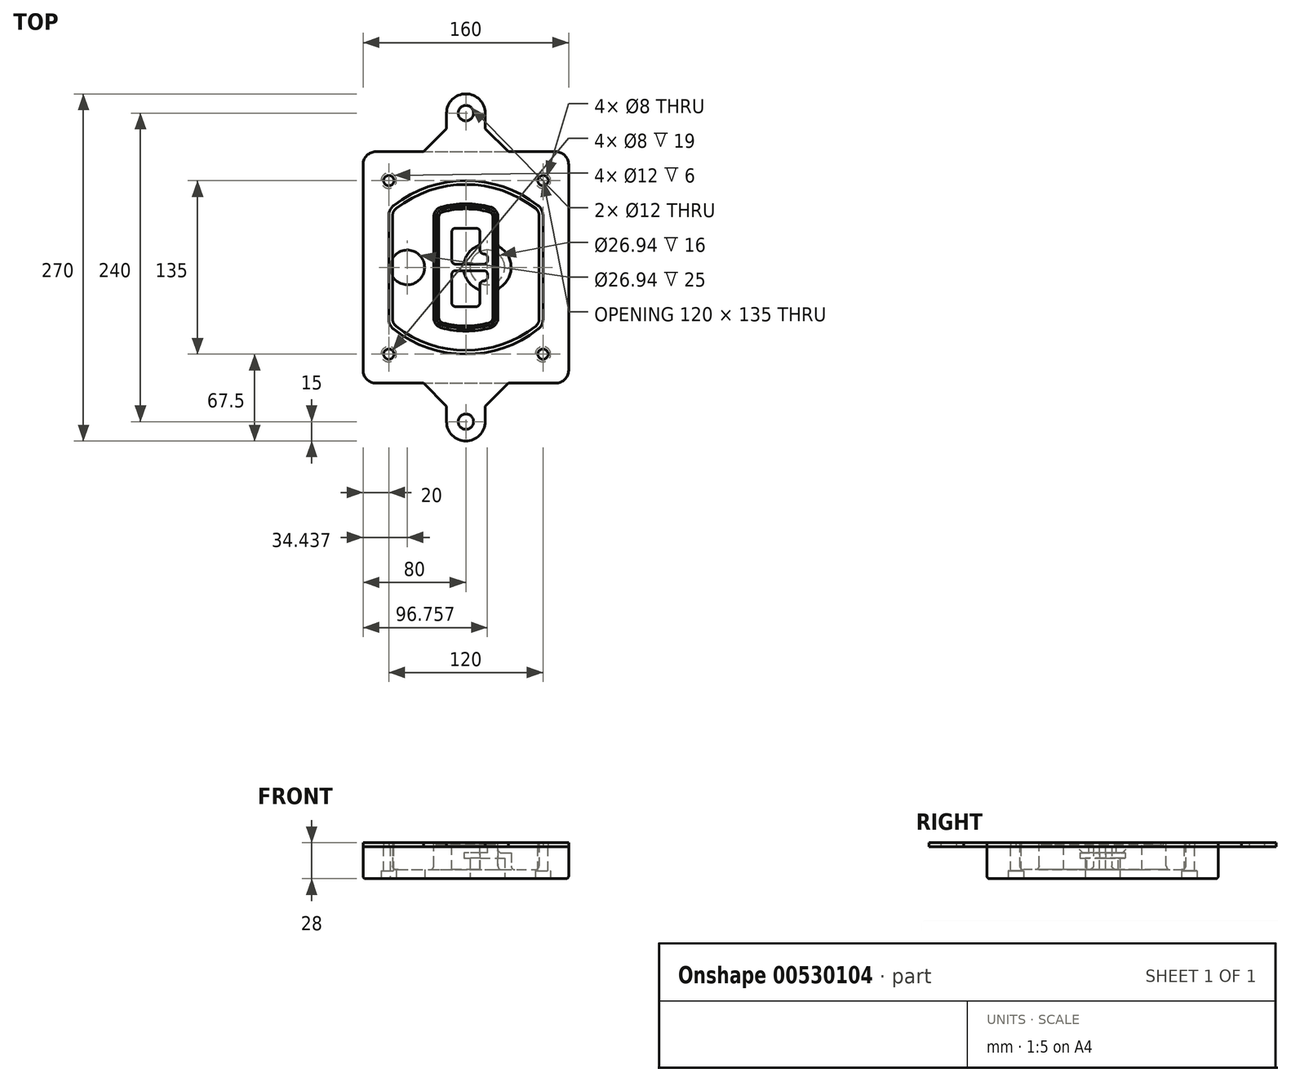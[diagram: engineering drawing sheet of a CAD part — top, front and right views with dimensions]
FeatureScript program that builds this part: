
annotation { "Feature Type Name" : "Feature", "Feature Type Description" : "" }
export const myFeature = defineFeature(function(context is Context, id is Id, definition is map)
    precondition{}
    {
        {
            var Q0;
            Q0=qCreatedBy(makeId("Top.planeOp"),FACE);
            var sketch = newSketch(context, id + "F0", { "sketchPlane" : qUnion([Q0])});
            skPoint(sketch, "E0.rect.middle", {"position": v(0, 0) * mm});
            skLineSegment(sketch, "E1.bottom", {"start": v(-70, -90) * mm, "end": v(70, -90) * mm});
            skLineSegment(sketch, "E1.top", {"start": v(-70, 90) * mm, "end": v(70, 90) * mm});
            skLineSegment(sketch, "E1.left", {"start": v(-80, -80) * mm, "end": v(-80, 80) * mm});
            skLineSegment(sketch, "E1.right", {"start": v(80, -80) * mm, "end": v(80, 80) * mm});
            skLineSegment(sketch, "E2", {"start": v(-80, 90) * mm, "end": v(80, -90) * mm, "construction": true});
            skLineSegment(sketch, "E3", {"start": v(80, 90) * mm, "end": v(-80, -90) * mm, "construction": true});
            skCircle(sketch, "E4", {"center": v(-60, 67.5) * mm, "radius": 4 * mm});
            skCircle(sketch, "E5", {"center": v(60, 67.5) * mm, "radius": 4 * mm});
            skCircle(sketch, "E6", {"center": v(60, -67.5) * mm, "radius": 4 * mm});
            skCircle(sketch, "E7", {"center": v(-60, -67.5) * mm, "radius": 4 * mm});
            skLineSegment(sketch, "E8", {"start": v(-60, 67.5) * mm, "end": v(60, 67.5) * mm, "construction": true});
            skLineSegment(sketch, "E9", {"start": v(60, 67.5) * mm, "end": v(60, -67.5) * mm, "construction": true});
            skLineSegment(sketch, "E10", {"start": v(60, -67.5) * mm, "end": v(-60, -67.5) * mm, "construction": true});
            skLineSegment(sketch, "E11", {"start": v(-60, -67.5) * mm, "end": v(-60, 67.5) * mm, "construction": true});
            skLineSegment(sketch, "E12", {"start": v(-60, 40.3) * mm, "end": v(-60, -40.3) * mm});
            skLineSegment(sketch, "E13", {"start": v(60, 40.3) * mm, "end": v(60, -40.3) * mm});
            skArc(sketch, "E14", {"start": v(56.15, 48.18) * mm, "mid": v(0, 67.5) * mm, "end": v(-56.15, 48.18) * mm});
            skArc(sketch, "E15", {"start": v(-56.15, -48.18) * mm, "mid": v(0, -67.5) * mm, "end": v(56.15, -48.18) * mm});
            skLineSegment(sketch, "E16", {"start": v(-60, 0) * mm, "end": v(60, 0) * mm, "construction": true});
            skPoint(sketch, "E17.visualSharp", {"position": v(-60, -45) * mm});
            skArc(sketch, "E17.filletArc", {"start": v(-60, -40.3) * mm, "mid": v(-58.99, -44.68) * mm, "end": v(-56.15, -48.18) * mm});
            skPoint(sketch, "E18.visualSharp", {"position": v(-60, 45) * mm});
            skArc(sketch, "E18.filletArc", {"start": v(-56.15, 48.18) * mm, "mid": v(-58.99, 44.68) * mm, "end": v(-60, 40.3) * mm});
            skPoint(sketch, "E19.visualSharp", {"position": v(60, 45) * mm});
            skArc(sketch, "E19.filletArc", {"start": v(60, 40.3) * mm, "mid": v(58.99, 44.68) * mm, "end": v(56.15, 48.18) * mm});
            skPoint(sketch, "E20.visualSharp", {"position": v(60, -45) * mm});
            skArc(sketch, "E20.filletArc", {"start": v(56.15, -48.18) * mm, "mid": v(58.99, -44.68) * mm, "end": v(60, -40.3) * mm});
            skPoint(sketch, "E21.visualSharp", {"position": v(-80, 90) * mm});
            skArc(sketch, "E21.filletArc", {"start": v(-70, 90) * mm, "mid": v(-77.07, 87.07) * mm, "end": v(-80, 80) * mm});
            skPoint(sketch, "E22.visualSharp", {"position": v(80, 90) * mm});
            skArc(sketch, "E22.filletArc", {"start": v(80, 80) * mm, "mid": v(77.07, 87.07) * mm, "end": v(70, 90) * mm});
            skPoint(sketch, "E23.visualSharp", {"position": v(80, -90) * mm});
            skArc(sketch, "E23.filletArc", {"start": v(70, -90) * mm, "mid": v(77.07, -87.07) * mm, "end": v(80, -80) * mm});
            skPoint(sketch, "E24.visualSharp", {"position": v(-80, -90) * mm});
            skArc(sketch, "E24.filletArc", {"start": v(-80, -80) * mm, "mid": v(-77.07, -87.07) * mm, "end": v(-70, -90) * mm});
            skArc(sketch, "E25.0", {"start": v(57, 40.3) * mm, "mid": v(56.3, 43.36) * mm, "end": v(54.3, 45.81) * mm});
            skLineSegment(sketch, "E25.1", {"start": v(57, 40.3) * mm, "end": v(57, -40.3) * mm});
            skArc(sketch, "E25.2", {"start": v(54.3, -45.81) * mm, "mid": v(56.3, -43.36) * mm, "end": v(57, -40.3) * mm});
            skArc(sketch, "E25.3", {"start": v(-54.3, -45.81) * mm, "mid": v(0, -64.5) * mm, "end": v(54.3, -45.81) * mm});
            skArc(sketch, "E25.4", {"start": v(-57, -40.3) * mm, "mid": v(-56.3, -43.36) * mm, "end": v(-54.3, -45.81) * mm});
            skArc(sketch, "E25.5", {"start": v(54.3, 45.81) * mm, "mid": v(0, 64.5) * mm, "end": v(-54.3, 45.81) * mm});
            skLineSegment(sketch, "E25.6", {"start": v(-57, 40.3) * mm, "end": v(-57, -40.3) * mm});
            skArc(sketch, "E25.7", {"start": v(-54.3, 45.81) * mm, "mid": v(-56.3, 43.36) * mm, "end": v(-57, 40.3) * mm});
            skArc(sketch, "E26.0", {"start": v(-58.62, 51.33) * mm, "mid": v(-62.58, 46.43) * mm, "end": v(-64, 40.3) * mm});
            skArc(sketch, "E26.1", {"start": v(58.62, 51.33) * mm, "mid": v(0, 71.5) * mm, "end": v(-58.62, 51.33) * mm});
            skArc(sketch, "E26.2", {"start": v(64, 40.3) * mm, "mid": v(62.58, 46.43) * mm, "end": v(58.62, 51.33) * mm});
            skLineSegment(sketch, "E26.3", {"start": v(64, 40.3) * mm, "end": v(64, -40.3) * mm});
            skArc(sketch, "E26.4", {"start": v(58.62, -51.33) * mm, "mid": v(62.58, -46.43) * mm, "end": v(64, -40.3) * mm});
            skLineSegment(sketch, "E26.5", {"start": v(-64, 40.3) * mm, "end": v(-64, -40.3) * mm});
            skArc(sketch, "E26.6", {"start": v(-58.62, -51.33) * mm, "mid": v(0, -71.5) * mm, "end": v(58.62, -51.33) * mm});
            skArc(sketch, "E26.7", {"start": v(-64, -40.3) * mm, "mid": v(-62.58, -46.43) * mm, "end": v(-58.62, -51.33) * mm});
            skSolve(sketch);
        }
        {
            var Q0;
            Q0=makeQuery(id+"F0.imprint","IMPRINT",FACE,{"disambiguationData":[TD([[makeQuery(id+"F0.imprint","IMPRINT",EDGE,{"derivedFrom":sQuery(id+"F0.wireOp",EDGE,"E1.bottom")}),1.0]])]});
            var Q1;
            Q1=makeQuery(id+"F0.imprint","IMPRINT",FACE,{"disambiguationData":[TD([[makeQuery(id+"F0.imprint","IMPRINT",EDGE,{"derivedFrom":sQuery(id+"F0.wireOp",EDGE,"E12")}),1.0]])]});
            var Q2;
            Q2=makeQuery(id+"F0.imprint","IMPRINT",FACE,{"disambiguationData":[TD([[makeQuery(id+"F0.imprint","IMPRINT",EDGE,{"derivedFrom":sQuery(id+"F0.wireOp",EDGE,"E25.0")}),1.0]])]});
            var Q3;
            Q3=makeQuery(id+"F0.imprint","IMPRINT",FACE,{"disambiguationData":[TD([[makeQuery(id+"F0.imprint","IMPRINT",EDGE,{"derivedFrom":sQuery(id+"F0.wireOp",EDGE,"E12")}),-1.0]])]});
            extrude(context, id + "F1", {"entities" : qUnion([Q0, Q1, Q2, Q3]), "oppositeDirection" : true, "depth" : 25 * mm});
        }
        {
            var Q0;
            Q0=makeQuery(id+"F0.imprint","IMPRINT",FACE,{"disambiguationData":[TD([[makeQuery(id+"F0.imprint","IMPRINT",EDGE,{"derivedFrom":sQuery(id+"F0.wireOp",EDGE,"E12")}),1.0]])]});
            extrude(context, id + "F2", {"entities" : qUnion([Q0]), "operationType" : NewBodyOperationType.ADD, "depth" : 3 * mm});
        }
        {
            var Q0;
            Q0=makeQuery(id+"F0.imprint","IMPRINT",FACE,{"disambiguationData":[TD([[makeQuery(id+"F0.imprint","IMPRINT",EDGE,{"derivedFrom":sQuery(id+"F0.wireOp",EDGE,"E25.0")}),1.0]])]});
            extrude(context, id + "F3", {"entities" : qUnion([Q0]), "operationType" : NewBodyOperationType.REMOVE, "oppositeDirection" : true, "depth" : 18 * mm});
        }
        {
            var Q0;
            Q0=makeQuery(id+"F2.opExtrude","CAP_FACE",FACE,{"disambiguationData":[OSD([sQuery(id+"F0.wireOp",EDGE,"E12"),sQuery(id+"F0.wireOp",EDGE,"E13"),sQuery(id+"F0.wireOp",EDGE,"E14"),sQuery(id+"F0.wireOp",EDGE,"E15"),sQuery(id+"F0.wireOp",EDGE,"E17.filletArc"),sQuery(id+"F0.wireOp",EDGE,"E18.filletArc"),sQuery(id+"F0.wireOp",EDGE,"E19.filletArc"),sQuery(id+"F0.wireOp",EDGE,"E20.filletArc"),sQuery(id+"F0.wireOp",EDGE,"E25.0"),sQuery(id+"F0.wireOp",EDGE,"E25.1"),sQuery(id+"F0.wireOp",EDGE,"E25.2"),sQuery(id+"F0.wireOp",EDGE,"E25.3"),sQuery(id+"F0.wireOp",EDGE,"E25.4"),sQuery(id+"F0.wireOp",EDGE,"E25.5"),sQuery(id+"F0.wireOp",EDGE,"E25.6"),sQuery(id+"F0.wireOp",EDGE,"E25.7")])],"isStart":false});
            var sketch = newSketch(context, id + "F4", { "sketchPlane" : qUnion([Q0])});
            skArc(sketch, "E27.0", {"start": v(-19.08, -46.97) * mm, "mid": v(0, -49.5) * mm, "end": v(19.08, -46.97) * mm});
            skArc(sketch, "E28.0", {"start": v(19.08, 46.97) * mm, "mid": v(0, 49.5) * mm, "end": v(-19.08, 46.97) * mm});
            skLineSegment(sketch, "E29", {"start": v(-25, 39.25) * mm, "end": v(-25, -39.25) * mm});
            skLineSegment(sketch, "E30", {"start": v(25, 39.25) * mm, "end": v(25, -39.25) * mm});
            skLineSegment(sketch, "E31", {"start": v(-25, 45.1) * mm, "end": v(25, 45.1) * mm, "construction": true});
            skLineSegment(sketch, "E32", {"start": v(-25, -45.1) * mm, "end": v(25, -45.1) * mm, "construction": true});
            skPoint(sketch, "E33.visualSharp", {"position": v(-25, 45.1) * mm});
            skArc(sketch, "E33.filletArc", {"start": v(-19.08, 46.97) * mm, "mid": v(-23.35, 44.11) * mm, "end": v(-25, 39.25) * mm});
            skPoint(sketch, "E34.visualSharp", {"position": v(25, 45.1) * mm});
            skArc(sketch, "E34.filletArc", {"start": v(25, 39.25) * mm, "mid": v(23.35, 44.11) * mm, "end": v(19.08, 46.97) * mm});
            skPoint(sketch, "E35.visualSharp", {"position": v(25, -45.1) * mm});
            skArc(sketch, "E35.filletArc", {"start": v(19.08, -46.97) * mm, "mid": v(23.35, -44.11) * mm, "end": v(25, -39.25) * mm});
            skPoint(sketch, "E36.visualSharp", {"position": v(-25, -45.1) * mm});
            skArc(sketch, "E36.filletArc", {"start": v(-25, -39.25) * mm, "mid": v(-23.35, -44.11) * mm, "end": v(-19.08, -46.97) * mm});
            skArc(sketch, "E37.0", {"start": v(54.3, 45.81) * mm, "mid": v(0, 64.5) * mm, "end": v(-54.3, 45.81) * mm});
            skArc(sketch, "E37.1", {"start": v(-54.3, 45.81) * mm, "mid": v(-56.3, 43.36) * mm, "end": v(-57, 40.3) * mm});
            skLineSegment(sketch, "E37.2", {"start": v(-57, 40.3) * mm, "end": v(-57, -40.3) * mm});
            skArc(sketch, "E37.3", {"start": v(-57, -40.3) * mm, "mid": v(-56.3, -43.36) * mm, "end": v(-54.3, -45.81) * mm});
            skArc(sketch, "E37.4", {"start": v(-54.3, -45.81) * mm, "mid": v(0, -64.5) * mm, "end": v(54.3, -45.81) * mm});
            skArc(sketch, "E37.5", {"start": v(54.3, -45.81) * mm, "mid": v(56.3, -43.36) * mm, "end": v(57, -40.3) * mm});
            skLineSegment(sketch, "E37.6", {"start": v(57, 40.3) * mm, "end": v(57, -40.3) * mm});
            skArc(sketch, "E37.7", {"start": v(57, 40.3) * mm, "mid": v(56.3, 43.36) * mm, "end": v(54.3, 45.81) * mm});
            skLineSegment(sketch, "E38.0", {"start": v(23, 39.25) * mm, "end": v(23, -39.25) * mm});
            skArc(sketch, "E38.1", {"start": v(18.56, -45.04) * mm, "mid": v(21.76, -42.9) * mm, "end": v(23, -39.25) * mm});
            skArc(sketch, "E38.2", {"start": v(-18.56, -45.04) * mm, "mid": v(0, -47.5) * mm, "end": v(18.56, -45.04) * mm});
            skArc(sketch, "E38.3", {"start": v(-23, -39.25) * mm, "mid": v(-21.76, -42.9) * mm, "end": v(-18.56, -45.04) * mm});
            skLineSegment(sketch, "E38.4", {"start": v(-23, 39.25) * mm, "end": v(-23, -39.25) * mm});
            skArc(sketch, "E38.5", {"start": v(23, 39.25) * mm, "mid": v(21.76, 42.9) * mm, "end": v(18.56, 45.04) * mm});
            skArc(sketch, "E38.6", {"start": v(-18.56, 45.04) * mm, "mid": v(-21.76, 42.9) * mm, "end": v(-23, 39.25) * mm});
            skArc(sketch, "E38.7", {"start": v(18.56, 45.04) * mm, "mid": v(0, 47.5) * mm, "end": v(-18.56, 45.04) * mm});
            skArc(sketch, "E39.0", {"start": v(21, 39.25) * mm, "mid": v(20.18, 41.68) * mm, "end": v(18.04, 43.1) * mm});
            skLineSegment(sketch, "E39.1", {"start": v(21, 39.25) * mm, "end": v(21, -39.25) * mm});
            skArc(sketch, "E39.2", {"start": v(18.04, -43.1) * mm, "mid": v(20.18, -41.68) * mm, "end": v(21, -39.25) * mm});
            skArc(sketch, "E39.3", {"start": v(-18.04, -43.1) * mm, "mid": v(0, -45.5) * mm, "end": v(18.04, -43.1) * mm});
            skArc(sketch, "E39.4", {"start": v(-21, -39.25) * mm, "mid": v(-20.18, -41.68) * mm, "end": v(-18.04, -43.1) * mm});
            skArc(sketch, "E39.5", {"start": v(18.04, 43.1) * mm, "mid": v(0, 45.5) * mm, "end": v(-18.04, 43.1) * mm});
            skLineSegment(sketch, "E39.6", {"start": v(-21, 39.25) * mm, "end": v(-21, -39.25) * mm});
            skArc(sketch, "E39.7", {"start": v(-18.04, 43.1) * mm, "mid": v(-20.18, 41.68) * mm, "end": v(-21, 39.25) * mm});
            skLineSegment(sketch, "E40", {"start": v(-25, 0) * mm, "end": v(25, 0) * mm, "construction": true});
            skLineSegment(sketch, "E41", {"start": v(-11, 5.5) * mm, "end": v(-11, 27.5) * mm});
            skLineSegment(sketch, "E42", {"start": v(-8, 30.5) * mm, "end": v(8, 30.5) * mm});
            skLineSegment(sketch, "E43", {"start": v(11, 27.5) * mm, "end": v(11, 13.5) * mm});
            skLineSegment(sketch, "E44", {"start": v(14, 10.5) * mm, "end": v(14, 10.5) * mm});
            skLineSegment(sketch, "E45", {"start": v(17, 7.5) * mm, "end": v(17, 5.5) * mm});
            skLineSegment(sketch, "E46", {"start": v(14, 2.5) * mm, "end": v(-8, 2.5) * mm});
            skPoint(sketch, "E47.visualSharp", {"position": v(-11, 30.5) * mm});
            skArc(sketch, "E47.filletArc", {"start": v(-8, 30.5) * mm, "mid": v(-10.12, 29.62) * mm, "end": v(-11, 27.5) * mm});
            skPoint(sketch, "E48.visualSharp", {"position": v(11, 30.5) * mm});
            skArc(sketch, "E48.filletArc", {"start": v(11, 27.5) * mm, "mid": v(10.12, 29.62) * mm, "end": v(8, 30.5) * mm});
            skPoint(sketch, "E49.visualSharp", {"position": v(11, 10.5) * mm});
            skArc(sketch, "E49.filletArc", {"start": v(11, 13.5) * mm, "mid": v(11.88, 11.38) * mm, "end": v(14, 10.5) * mm});
            skPoint(sketch, "E50.visualSharp", {"position": v(17, 10.5) * mm});
            skArc(sketch, "E50.filletArc", {"start": v(17, 7.5) * mm, "mid": v(16.12, 9.62) * mm, "end": v(14, 10.5) * mm});
            skPoint(sketch, "E51.visualSharp", {"position": v(17, 2.5) * mm});
            skArc(sketch, "E51.filletArc", {"start": v(14, 2.5) * mm, "mid": v(16.12, 3.38) * mm, "end": v(17, 5.5) * mm});
            skPoint(sketch, "E52.visualSharp", {"position": v(-11, 2.5) * mm});
            skArc(sketch, "E52.filletArc", {"start": v(-11, 5.5) * mm, "mid": v(-10.12, 3.38) * mm, "end": v(-8, 2.5) * mm});
            skLineSegment(sketch, "E53.0.MirrorCS", {"start": v(14, -2.5) * mm, "end": v(-8, -2.5) * mm});
            skArc(sketch, "E54.0.MirrorCS", {"start": v(-11, -5.5) * mm, "mid": v(-10.12, -3.38) * mm, "end": v(-8, -2.5) * mm});
            skLineSegment(sketch, "E55.0.MirrorCS", {"start": v(-11, -5.5) * mm, "end": v(-11, -27.5) * mm});
            skArc(sketch, "E56.0.MirrorCS", {"start": v(-8, -30.5) * mm, "mid": v(-10.12, -29.62) * mm, "end": v(-11, -27.5) * mm});
            skLineSegment(sketch, "E57.0.MirrorCS", {"start": v(-8, -30.5) * mm, "end": v(8, -30.5) * mm});
            skArc(sketch, "E58.0.MirrorCS", {"start": v(11, -27.5) * mm, "mid": v(10.12, -29.62) * mm, "end": v(8, -30.5) * mm});
            skLineSegment(sketch, "E59.0.MirrorCS", {"start": v(11, -27.5) * mm, "end": v(11, -13.5) * mm});
            skArc(sketch, "E60.0.MirrorCS", {"start": v(11, -13.5) * mm, "mid": v(11.88, -11.38) * mm, "end": v(14, -10.5) * mm});
            skArc(sketch, "E61.0.MirrorCS", {"start": v(17, -7.5) * mm, "mid": v(16.12, -9.62) * mm, "end": v(14, -10.5) * mm});
            skLineSegment(sketch, "E62.0.MirrorCS", {"start": v(17, -7.5) * mm, "end": v(17, -5.5) * mm});
            skArc(sketch, "E63.0.MirrorCS", {"start": v(14, -2.5) * mm, "mid": v(16.12, -3.38) * mm, "end": v(17, -5.5) * mm});
            skSolve(sketch);
        }
        {
            var Q0;
            Q0=makeQuery(id+"F4.imprint","IMPRINT",FACE,{"disambiguationData":[TD([[makeQuery(id+"F4.imprint","IMPRINT",EDGE,{"derivedFrom":sQuery(id+"F4.wireOp",EDGE,"E27.0")}),1.0]])]});
            var Q1;
            Q1=makeQuery(id+"F4.imprint","IMPRINT",FACE,{"disambiguationData":[TD([[makeQuery(id+"F4.imprint","IMPRINT",EDGE,{"derivedFrom":sQuery(id+"F4.wireOp",EDGE,"E38.0")}),-1.0]])]});
            var Q2;
            Q2=makeQuery(id+"F4.imprint","IMPRINT",FACE,{"disambiguationData":[TD([[makeQuery(id+"F4.imprint","IMPRINT",EDGE,{"derivedFrom":sQuery(id+"F4.wireOp",EDGE,"E39.0")}),1.0]])]});
            extrude(context, id + "F5", {"entities" : qUnion([Q0, Q1, Q2]), "operationType" : NewBodyOperationType.ADD, "endBound" : BoundingType.UP_TO_NEXT, "oppositeDirection" : true, "depth" : 25 * mm});
        }
        {
            var Q0;
            Q0=makeQuery(id+"F4.imprint","IMPRINT",FACE,{"disambiguationData":[TD([[makeQuery(id+"F4.imprint","IMPRINT",EDGE,{"derivedFrom":sQuery(id+"F4.wireOp",EDGE,"E38.0")}),-1.0]])]});
            extrude(context, id + "F6", {"entities" : qUnion([Q0]), "operationType" : NewBodyOperationType.REMOVE, "oppositeDirection" : true, "depth" : 2 * mm});
        }
        {
            var Q0;
            Q0=makeQuery(id+"F1.opExtrude","CAP_FACE",FACE,{"disambiguationData":[OSD([sQuery(id+"F0.wireOp",EDGE,"E1.bottom"),sQuery(id+"F0.wireOp",EDGE,"E1.top"),sQuery(id+"F0.wireOp",EDGE,"E1.left"),sQuery(id+"F0.wireOp",EDGE,"E1.right"),sQuery(id+"F0.wireOp",EDGE,"E4"),sQuery(id+"F0.wireOp",EDGE,"E5"),sQuery(id+"F0.wireOp",EDGE,"E6"),sQuery(id+"F0.wireOp",EDGE,"E7"),sQuery(id+"F0.wireOp",EDGE,"E21.filletArc"),sQuery(id+"F0.wireOp",EDGE,"E22.filletArc"),sQuery(id+"F0.wireOp",EDGE,"E23.filletArc"),sQuery(id+"F0.wireOp",EDGE,"E24.filletArc")])],"isStart":false});
            var sketch = newSketch(context, id + "F7", { "sketchPlane" : qUnion([Q0])});
            skCircle(sketch, "E64", {"center": v(16.76, 0) * mm, "radius": 13.47 * mm});
            skCircle(sketch, "E65", {"center": v(-45.56, 0) * mm, "radius": 13.47 * mm});
            skLineSegment(sketch, "E66", {"start": v(80, 0) * mm, "end": v(-80, 0) * mm});
            skCircle(sketch, "E67", {"center": v(16.76, 0) * mm, "radius": 18.47 * mm});
            skCircle(sketch, "E68", {"center": v(60, -67.5) * mm, "radius": 6 * mm});
            skCircle(sketch, "E69", {"center": v(-60, -67.5) * mm, "radius": 6 * mm});
            skCircle(sketch, "E70", {"center": v(-60, 67.5) * mm, "radius": 6 * mm});
            skCircle(sketch, "E71", {"center": v(60, 67.5) * mm, "radius": 6 * mm});
            skSolve(sketch);
        }
        {
            var Q0;
            {var subQ1=sQuery(id+"F7.wireOp",EDGE,"E66");var subQ4=sQuery(id+"F7.wireOp",EDGE,"E64");var subQ6=makeQuery(id+"F7.imprint","INTERSECT",VERTEX,{"disambiguationData":[OD(0.0)],"derivedFrom":[subQ4,subQ1]});Q0=makeQuery(id+"F7.imprint","IMPRINT",FACE,{"disambiguationData":[TD([[makeQuery(id+"F7.imprint","IMPRINT",EDGE,{"disambiguationData":[TD([[subQ6,-1.0]])],"derivedFrom":subQ4}),-1.0]])]});}
            var Q1;
            {var subQ0=sQuery(id+"F7.wireOp",EDGE,"E66");var subQ1=sQuery(id+"F7.wireOp",EDGE,"E64");var subQ3=makeQuery(id+"F7.imprint","INTERSECT",VERTEX,{"disambiguationData":[OD(0.0)],"derivedFrom":[subQ1,subQ0]});Q1=makeQuery(id+"F7.imprint","IMPRINT",FACE,{"disambiguationData":[TD([[makeQuery(id+"F7.imprint","IMPRINT",EDGE,{"disambiguationData":[TD([[subQ3,-1.0]])],"derivedFrom":subQ1}),1.0]])]});}
            var Q2;
            {var subQ0=sQuery(id+"F7.wireOp",EDGE,"E66");var subQ1=sQuery(id+"F7.wireOp",EDGE,"E64");var subQ3=makeQuery(id+"F7.imprint","INTERSECT",VERTEX,{"disambiguationData":[OD(0.0)],"derivedFrom":[subQ1,subQ0]});Q2=makeQuery(id+"F7.imprint","IMPRINT",FACE,{"disambiguationData":[TD([[makeQuery(id+"F7.imprint","IMPRINT",EDGE,{"disambiguationData":[TD([[subQ3,1.0]])],"derivedFrom":subQ1}),1.0]])]});}
            var Q3;
            {var subQ1=sQuery(id+"F7.wireOp",EDGE,"E66");var subQ4=sQuery(id+"F7.wireOp",EDGE,"E64");var subQ6=makeQuery(id+"F7.imprint","INTERSECT",VERTEX,{"disambiguationData":[OD(0.0)],"derivedFrom":[subQ4,subQ1]});Q3=makeQuery(id+"F7.imprint","IMPRINT",FACE,{"disambiguationData":[TD([[makeQuery(id+"F7.imprint","IMPRINT",EDGE,{"disambiguationData":[TD([[subQ6,1.0]])],"derivedFrom":subQ4}),-1.0]])]});}
            extrude(context, id + "F8", {"entities" : qUnion([Q0, Q1, Q2, Q3]), "operationType" : NewBodyOperationType.ADD, "oppositeDirection" : true, "depth" : 20 * mm});
        }
        {
            var Q0;
            {var subQ0=sQuery(id+"F7.wireOp",EDGE,"E66");var subQ1=sQuery(id+"F7.wireOp",EDGE,"E64");var subQ3=makeQuery(id+"F7.imprint","INTERSECT",VERTEX,{"disambiguationData":[OD(0.0)],"derivedFrom":[subQ1,subQ0]});Q0=makeQuery(id+"F7.imprint","IMPRINT",FACE,{"disambiguationData":[TD([[makeQuery(id+"F7.imprint","IMPRINT",EDGE,{"disambiguationData":[TD([[subQ3,-1.0]])],"derivedFrom":subQ1}),1.0]])]});}
            var Q1;
            {var subQ0=sQuery(id+"F7.wireOp",EDGE,"E66");var subQ1=sQuery(id+"F7.wireOp",EDGE,"E64");var subQ3=makeQuery(id+"F7.imprint","INTERSECT",VERTEX,{"disambiguationData":[OD(0.0)],"derivedFrom":[subQ1,subQ0]});Q1=makeQuery(id+"F7.imprint","IMPRINT",FACE,{"disambiguationData":[TD([[makeQuery(id+"F7.imprint","IMPRINT",EDGE,{"disambiguationData":[TD([[subQ3,1.0]])],"derivedFrom":subQ1}),1.0]])]});}
            extrude(context, id + "F9", {"entities" : qUnion([Q0, Q1]), "operationType" : NewBodyOperationType.REMOVE, "oppositeDirection" : true, "depth" : 16 * mm});
        }
        {
            var Q0;
            {var subQ0=sQuery(id+"F7.wireOp",EDGE,"E66");var subQ1=sQuery(id+"F7.wireOp",EDGE,"E65");var subQ3=makeQuery(id+"F7.imprint","INTERSECT",VERTEX,{"disambiguationData":[OD(0.0)],"derivedFrom":[subQ1,subQ0]});Q0=makeQuery(id+"F7.imprint","IMPRINT",FACE,{"disambiguationData":[TD([[makeQuery(id+"F7.imprint","IMPRINT",EDGE,{"disambiguationData":[TD([[subQ3,-1.0]])],"derivedFrom":subQ1}),1.0]])]});}
            var Q1;
            {var subQ0=sQuery(id+"F7.wireOp",EDGE,"E66");var subQ1=sQuery(id+"F7.wireOp",EDGE,"E65");var subQ3=makeQuery(id+"F7.imprint","INTERSECT",VERTEX,{"disambiguationData":[OD(0.0)],"derivedFrom":[subQ1,subQ0]});Q1=makeQuery(id+"F7.imprint","IMPRINT",FACE,{"disambiguationData":[TD([[makeQuery(id+"F7.imprint","IMPRINT",EDGE,{"disambiguationData":[TD([[subQ3,1.0]])],"derivedFrom":subQ1}),1.0]])]});}
            extrude(context, id + "F10", {"entities" : qUnion([Q0, Q1]), "operationType" : NewBodyOperationType.REMOVE, "oppositeDirection" : true, "depth" : 25 * mm});
        }
        {
            var Q0;
            Q0=makeQuery(id+"F7.imprint","IMPRINT",FACE,{"disambiguationData":[TD([[makeQuery(id+"F7.imprint","IMPRINT",EDGE,{"derivedFrom":sQuery(id+"F7.wireOp",EDGE,"E68")}),1.0]])]});
            var Q1;
            Q1=makeQuery(id+"F7.imprint","IMPRINT",FACE,{"disambiguationData":[TD([[makeQuery(id+"F7.imprint","IMPRINT",EDGE,{"derivedFrom":makeQuery(id+"F1.opExtrude","CAP_EDGE",EDGE,{"disambiguationData":[OSD([sQuery(id+"F0.wireOp",EDGE,"E5")])],"isStart":false})}),-1.0]])]});
            var Q2;
            Q2=makeQuery(id+"F7.imprint","IMPRINT",FACE,{"disambiguationData":[TD([[makeQuery(id+"F7.imprint","IMPRINT",EDGE,{"derivedFrom":sQuery(id+"F7.wireOp",EDGE,"E69")}),1.0]])]});
            var Q3;
            Q3=makeQuery(id+"F7.imprint","IMPRINT",FACE,{"disambiguationData":[TD([[makeQuery(id+"F7.imprint","IMPRINT",EDGE,{"derivedFrom":makeQuery(id+"F1.opExtrude","CAP_EDGE",EDGE,{"disambiguationData":[OSD([sQuery(id+"F0.wireOp",EDGE,"E4")])],"isStart":false})}),-1.0]])]});
            var Q4;
            Q4=makeQuery(id+"F7.imprint","IMPRINT",FACE,{"disambiguationData":[TD([[makeQuery(id+"F7.imprint","IMPRINT",EDGE,{"derivedFrom":sQuery(id+"F7.wireOp",EDGE,"E70")}),1.0]])]});
            var Q5;
            Q5=makeQuery(id+"F7.imprint","IMPRINT",FACE,{"disambiguationData":[TD([[makeQuery(id+"F7.imprint","IMPRINT",EDGE,{"derivedFrom":makeQuery(id+"F1.opExtrude","CAP_EDGE",EDGE,{"disambiguationData":[OSD([sQuery(id+"F0.wireOp",EDGE,"E7")])],"isStart":false})}),-1.0]])]});
            var Q6;
            Q6=makeQuery(id+"F7.imprint","IMPRINT",FACE,{"disambiguationData":[TD([[makeQuery(id+"F7.imprint","IMPRINT",EDGE,{"derivedFrom":sQuery(id+"F7.wireOp",EDGE,"E71")}),1.0]])]});
            var Q7;
            Q7=makeQuery(id+"F7.imprint","IMPRINT",FACE,{"disambiguationData":[TD([[makeQuery(id+"F7.imprint","IMPRINT",EDGE,{"derivedFrom":makeQuery(id+"F1.opExtrude","CAP_EDGE",EDGE,{"disambiguationData":[OSD([sQuery(id+"F0.wireOp",EDGE,"E6")])],"isStart":false})}),-1.0]])]});
            extrude(context, id + "F11", {"entities" : qUnion([Q0, Q1, Q2, Q3, Q4, Q5, Q6, Q7]), "operationType" : NewBodyOperationType.REMOVE, "oppositeDirection" : true, "depth" : 6 * mm});
        }
        {
            var Q0;
            Q0=makeQuery(id+"F9.boolean.opBoolean","COPY",FACE,{"derivedFrom":makeQuery(id+"F9.opExtrude","CAP_FACE",FACE,{"disambiguationData":[OSD([sQuery(id+"F7.wireOp",EDGE,"E64")])],"isStart":false})});
            var sketch = newSketch(context, id + "F12", { "sketchPlane" : qUnion([Q0])});
            skArc(sketch, "E72.0", {"start": v(11, 17.55) * mm, "mid": v(2.57, 11.82) * mm, "end": v(-1.54, 2.5) * mm});
            skArc(sketch, "E72.1", {"start": v(-1.54, -2.5) * mm, "mid": v(2.57, -11.82) * mm, "end": v(11, -17.55) * mm});
            skLineSegment(sketch, "E73", {"start": v(-1.54, -2.5) * mm, "end": v(14, -2.5) * mm});
            skLineSegment(sketch, "E74.0", {"start": v(14, 2.5) * mm, "end": v(-1.54, 2.5) * mm});
            skArc(sketch, "E74.1", {"start": v(14, 2.5) * mm, "mid": v(16.12, 3.38) * mm, "end": v(17, 5.5) * mm});
            skLineSegment(sketch, "E74.2", {"start": v(17, 7.5) * mm, "end": v(17, 5.5) * mm});
            skArc(sketch, "E74.3", {"start": v(17, 7.5) * mm, "mid": v(16.12, 9.62) * mm, "end": v(14, 10.5) * mm});
            skArc(sketch, "E74.4", {"start": v(11, 13.5) * mm, "mid": v(11.88, 11.38) * mm, "end": v(14, 10.5) * mm});
            skLineSegment(sketch, "E74.5", {"start": v(11, 17.55) * mm, "end": v(11, 13.5) * mm});
            skLineSegment(sketch, "E74.7", {"start": v(14, -2.5) * mm, "end": v(-1.54, -2.5) * mm});
            skArc(sketch, "E74.8", {"start": v(14, -2.5) * mm, "mid": v(16.12, -3.38) * mm, "end": v(17, -5.5) * mm});
            skLineSegment(sketch, "E74.9", {"start": v(17, -7.5) * mm, "end": v(17, -5.5) * mm});
            skArc(sketch, "E74.10", {"start": v(17, -7.5) * mm, "mid": v(16.12, -9.62) * mm, "end": v(14, -10.5) * mm});
            skArc(sketch, "E74.11", {"start": v(11, -13.5) * mm, "mid": v(11.88, -11.38) * mm, "end": v(14, -10.5) * mm});
            skLineSegment(sketch, "E74.12", {"start": v(11, -17.55) * mm, "end": v(11, -13.5) * mm});
            skPoint(sketch, "E75.orphan", {"position": v(11, -27.5) * mm});
            skPoint(sketch, "E76.orphan", {"position": v(-8, -2.5) * mm});
            skPoint(sketch, "E77.orphan", {"position": v(-8, 2.5) * mm});
            skPoint(sketch, "E78.orphan", {"position": v(11, 27.5) * mm});
            skSolve(sketch);
        }
        {
            var Q0;
            {var subQ7=sQuery(id+"F12.wireOp",EDGE,"E72.0");var subQ14=sQuery(id+"F12.wireOp",EDGE,"E72.1");var subQ16=sQuery(id+"F12.wireOp",EDGE,"E74.1");var subQ18=sQuery(id+"F12.wireOp",EDGE,"E74.8");Q0=qUnion([makeQuery(id+"F12.imprint","IMPRINT",FACE,{"disambiguationData":[TD([[makeQuery(id+"F12.imprint","IMPRINT",EDGE,{"derivedFrom":subQ7}),1.0]])]}),makeQuery(id+"F12.imprint","IMPRINT",FACE,{"disambiguationData":[TD([[makeQuery(id+"F12.imprint","IMPRINT",EDGE,{"derivedFrom":subQ14}),1.0]])]}),makeQuery(id+"F12.imprint","IMPRINT",FACE,{"disambiguationData":[TD([[makeQuery(id+"F12.imprint","IMPRINT",EDGE,{"derivedFrom":subQ16}),1.0]])]}),makeQuery(id+"F12.imprint","IMPRINT",FACE,{"disambiguationData":[TD([[makeQuery(id+"F12.imprint","IMPRINT",EDGE,{"derivedFrom":subQ18}),-1.0]])]})]);}
            var Q1;
            Q1=makeQuery(id+"F5.boolean.opBoolean","SPLIT",FACE,{"disambiguationData":[TD([makeQuery(id+"F5.opExtrude","SWEPT_FACE",FACE,{"disambiguationData":[OSD([sQuery(id+"F4.wireOp",EDGE,"E41")])]})])],"derivedFrom":makeQuery(id+"F3.boolean.opBoolean","COPY",FACE,{"derivedFrom":makeQuery(id+"F3.opExtrude","CAP_FACE",FACE,{"disambiguationData":[OSD([sQuery(id+"F0.wireOp",EDGE,"E25.0"),sQuery(id+"F0.wireOp",EDGE,"E25.1"),sQuery(id+"F0.wireOp",EDGE,"E25.2"),sQuery(id+"F0.wireOp",EDGE,"E25.3"),sQuery(id+"F0.wireOp",EDGE,"E25.4"),sQuery(id+"F0.wireOp",EDGE,"E25.5"),sQuery(id+"F0.wireOp",EDGE,"E25.6"),sQuery(id+"F0.wireOp",EDGE,"E25.7")])],"isStart":false})})});
            extrude(context, id + "F13", {"entities" : qUnion([Q0]), "operationType" : NewBodyOperationType.REMOVE, "endBound" : BoundingType.UP_TO_SURFACE, "endBoundEntityFace" : qUnion([Q1]), "depth" : 25 * mm});
        }
        {
            var Q0;
            Q0=makeQuery(id+"F3.boolean.opBoolean","COPY",EDGE,{"derivedFrom":makeQuery(id+"F3.opExtrude","CAP_EDGE",EDGE,{"disambiguationData":[OSD([sQuery(id+"F0.wireOp",EDGE,"E25.6")])],"isStart":false})});
            var Q1;
            Q1=makeQuery(id+"F8.boolean.opBoolean","INTERSECT",EDGE,{"derivedFrom":[makeQuery(id+"F5.opExtrude","SWEPT_FACE",FACE,{"disambiguationData":[OSD([sQuery(id+"F4.wireOp",EDGE,"E30")])]}),makeQuery(id+"F8.opExtrude","CAP_FACE",FACE,{"disambiguationData":[OSD([sQuery(id+"F7.wireOp",EDGE,"E67")])],"isStart":false})]});
            var Q2;
            Q2=makeQuery(id+"F8.boolean.opBoolean","INTERSECT",EDGE,{"disambiguationData":[OD(1.0)],"derivedFrom":[makeQuery(id+"F5.opExtrude","SWEPT_FACE",FACE,{"disambiguationData":[OSD([sQuery(id+"F4.wireOp",EDGE,"E30")])]}),makeQuery(id+"F8.opExtrude","SWEPT_FACE",FACE,{"disambiguationData":[OSD([sQuery(id+"F7.wireOp",EDGE,"E67")])]})]});
            var Q3;
            {var subQ0=sQuery(id+"F4.wireOp",EDGE,"E30");Q3=makeQuery(id+"F8.boolean.opBoolean","SPLIT",EDGE,{"disambiguationData":[TD([makeQuery(id+"F5.opExtrude","SWEPT_FACE",FACE,{"disambiguationData":[OSD([sQuery(id+"F4.wireOp",EDGE,"E35.filletArc")])]})])],"derivedFrom":makeQuery(id+"F5.opExtrude","CAP_EDGE",EDGE,{"disambiguationData":[OSD([subQ0])],"isStart":false})});}
            var Q4;
            {var subQ0=sQuery(id+"F0.wireOp",EDGE,"E25.7");var subQ1=sQuery(id+"F0.wireOp",EDGE,"E25.1");var subQ2=sQuery(id+"F0.wireOp",EDGE,"E25.6");var subQ3=sQuery(id+"F0.wireOp",EDGE,"E25.5");var subQ4=sQuery(id+"F0.wireOp",EDGE,"E25.4");var subQ5=sQuery(id+"F0.wireOp",EDGE,"E25.0");var subQ6=sQuery(id+"F0.wireOp",EDGE,"E25.2");var subQ7=sQuery(id+"F0.wireOp",EDGE,"E25.3");Q4=makeQuery(id+"F8.boolean.opBoolean","INTERSECT",EDGE,{"derivedFrom":[makeQuery(id+"F5.boolean.opBoolean","SPLIT",FACE,{"disambiguationData":[TD([makeQuery(id+"F2.opExtrude","SWEPT_FACE",FACE,{"disambiguationData":[OSD([subQ5])]})])],"derivedFrom":makeQuery(id+"F3.boolean.opBoolean","COPY",FACE,{"derivedFrom":makeQuery(id+"F3.opExtrude","CAP_FACE",FACE,{"disambiguationData":[OSD([subQ5,subQ1,subQ6,subQ7,subQ4,subQ3,subQ2,subQ0])],"isStart":false})})}),makeQuery(id+"F8.opExtrude","SWEPT_FACE",FACE,{"disambiguationData":[OSD([sQuery(id+"F7.wireOp",EDGE,"E67")])]})]});}
            var Q5;
            Q5=makeQuery(id+"F8.boolean.opBoolean","INTERSECT",EDGE,{"disambiguationData":[OD(0.0)],"derivedFrom":[makeQuery(id+"F5.opExtrude","SWEPT_FACE",FACE,{"disambiguationData":[OSD([sQuery(id+"F4.wireOp",EDGE,"E30")])]}),makeQuery(id+"F8.opExtrude","SWEPT_FACE",FACE,{"disambiguationData":[OSD([sQuery(id+"F7.wireOp",EDGE,"E67")])]})]});
            fillet(context, id + "F14", {"entities" : qUnion([Q0, Q1, Q2, Q3, Q4, Q5]), "radius" : 3 * mm, "tangentPropagation" : true, "allowEdgeOverflow" : false});
        }
        {
            var Q0;
            Q0=makeQuery(id+"F1.opExtrude","CAP_EDGE",EDGE,{"disambiguationData":[OSD([sQuery(id+"F0.wireOp",EDGE,"E1.bottom")])],"isStart":false});
            fillet(context, id + "F15", {"entities" : qUnion([Q0]), "radius" : 2 * mm, "tangentPropagation" : true, "allowEdgeOverflow" : false});
        }
        {
            var Q0;
            {var subQ0=sQuery(id+"F0.wireOp",EDGE,"E21.filletArc");var subQ1=sQuery(id+"F0.wireOp",EDGE,"E7");var subQ2=sQuery(id+"F0.wireOp",EDGE,"E6");var subQ3=sQuery(id+"F0.wireOp",EDGE,"E5");var subQ4=sQuery(id+"F0.wireOp",EDGE,"E4");var subQ5=sQuery(id+"F0.wireOp",EDGE,"E22.filletArc");var subQ6=sQuery(id+"F0.wireOp",EDGE,"E1.bottom");var subQ7=sQuery(id+"F0.wireOp",EDGE,"E1.right");var subQ8=sQuery(id+"F0.wireOp",EDGE,"E1.top");var subQ9=sQuery(id+"F0.wireOp",EDGE,"E1.left");var subQ10=sQuery(id+"F0.wireOp",EDGE,"E23.filletArc");var subQ11=sQuery(id+"F0.wireOp",EDGE,"E24.filletArc");Q0=makeQuery(id+"F2.boolean.opBoolean","SPLIT",FACE,{"disambiguationData":[TD([makeQuery(id+"F1.opExtrude","SWEPT_FACE",FACE,{"disambiguationData":[OSD([subQ6])]})])],"derivedFrom":makeQuery(id+"F1.opExtrude","CAP_FACE",FACE,{"disambiguationData":[OSD([subQ6,subQ8,subQ9,subQ7,subQ4,subQ3,subQ2,subQ1,subQ0,subQ5,subQ10,subQ11])],"isStart":true})});}
            var sketch = newSketch(context, id + "F16", { "sketchPlane" : qUnion([Q0])});
            skLineSegment(sketch, "E79", {"start": v(0, 90) * mm, "end": v(0, 120) * mm, "construction": true});
            skPoint(sketch, "E79.endSnap0", {"position": v(0, 90) * mm});
            skCircle(sketch, "E80", {"center": v(0, 120) * mm, "radius": 6 * mm});
            skLineSegment(sketch, "E81", {"start": v(-33, 90) * mm, "end": v(-15, 108) * mm});
            skLineSegment(sketch, "E82", {"start": v(-15, 108) * mm, "end": v(-15, 120) * mm});
            skArc(sketch, "E83", {"start": v(15, 120) * mm, "mid": v(0, 135) * mm, "end": v(-15, 120) * mm});
            skLineSegment(sketch, "E84.0", {"start": v(-70, 90) * mm, "end": v(70, 90) * mm});
            skArc(sketch, "E84.1", {"start": v(-70, 90) * mm, "mid": v(-77.07, 87.07) * mm, "end": v(-80, 80) * mm});
            skLineSegment(sketch, "E85.0", {"start": v(-80, -80) * mm, "end": v(-80, 80) * mm});
            skArc(sketch, "E85.1", {"start": v(-80, -80) * mm, "mid": v(-77.07, -87.07) * mm, "end": v(-70, -90) * mm});
            skLineSegment(sketch, "E85.2", {"start": v(-70, -90) * mm, "end": v(70, -90) * mm});
            skArc(sketch, "E85.3", {"start": v(70, -90) * mm, "mid": v(77.07, -87.07) * mm, "end": v(80, -80) * mm});
            skLineSegment(sketch, "E85.4", {"start": v(80, -80) * mm, "end": v(80, 80) * mm});
            skArc(sketch, "E85.5", {"start": v(80, 80) * mm, "mid": v(77.07, 87.07) * mm, "end": v(70, 90) * mm});
            skArc(sketch, "E85.6", {"start": v(56.15, 48.18) * mm, "mid": v(0, 67.5) * mm, "end": v(-56.15, 48.18) * mm});
            skArc(sketch, "E85.7", {"start": v(-56.15, 48.18) * mm, "mid": v(-58.99, 44.68) * mm, "end": v(-60, 40.3) * mm});
            skLineSegment(sketch, "E85.8", {"start": v(-60, 40.3) * mm, "end": v(-60, -40.3) * mm});
            skArc(sketch, "E85.9", {"start": v(60, 40.3) * mm, "mid": v(58.99, 44.68) * mm, "end": v(56.15, 48.18) * mm});
            skLineSegment(sketch, "E85.10", {"start": v(60, 40.3) * mm, "end": v(60, -40.3) * mm});
            skArc(sketch, "E85.11", {"start": v(56.15, -48.18) * mm, "mid": v(58.99, -44.68) * mm, "end": v(60, -40.3) * mm});
            skArc(sketch, "E85.12", {"start": v(-56.15, -48.18) * mm, "mid": v(0, -67.5) * mm, "end": v(56.15, -48.18) * mm});
            skArc(sketch, "E85.13", {"start": v(-60, -40.3) * mm, "mid": v(-58.99, -44.68) * mm, "end": v(-56.15, -48.18) * mm});
            skCircle(sketch, "E85.14", {"center": v(-60, 67.5) * mm, "radius": 4 * mm});
            skCircle(sketch, "E85.15", {"center": v(60, 67.5) * mm, "radius": 4 * mm});
            skCircle(sketch, "E85.16", {"center": v(60, -67.5) * mm, "radius": 4 * mm});
            skCircle(sketch, "E85.17", {"center": v(-60, -67.5) * mm, "radius": 4 * mm});
            skLineSegment(sketch, "E86", {"start": v(15, 120) * mm, "end": v(15, 108) * mm});
            skLineSegment(sketch, "E87", {"start": v(15, 108) * mm, "end": v(33, 90) * mm});
            skLineSegment(sketch, "E88", {"start": v(-80, 0) * mm, "end": v(80, 0) * mm, "construction": true});
            skLineSegment(sketch, "E89.MirrorCS", {"start": v(15, -108) * mm, "end": v(33, -90) * mm});
            skLineSegment(sketch, "E90.MirrorCS", {"start": v(15, -120) * mm, "end": v(15, -108) * mm});
            skArc(sketch, "E91.MirrorCS", {"start": v(15, -120) * mm, "mid": v(0, -135) * mm, "end": v(-15, -120) * mm});
            skLineSegment(sketch, "E92.MirrorCS", {"start": v(-15, -108) * mm, "end": v(-15, -120) * mm});
            skLineSegment(sketch, "E93.MirrorCS", {"start": v(-33, -90) * mm, "end": v(-15, -108) * mm});
            skLineSegment(sketch, "E94.MirrorCS", {"start": v(0, -90) * mm, "end": v(0, -120) * mm, "construction": true});
            skCircle(sketch, "E95.MirrorC", {"center": v(0, -120) * mm, "radius": 6 * mm});
            skSolve(sketch);
        }
        {
            var Q0;
            Q0 = qSketchRegion(id + "F16", true);
            var Q1;
            Q1=makeQuery(id+"F2.opExtrude","CAP_FACE",FACE,{"disambiguationData":[OSD([sQuery(id+"F0.wireOp",EDGE,"E12"),sQuery(id+"F0.wireOp",EDGE,"E13"),sQuery(id+"F0.wireOp",EDGE,"E14"),sQuery(id+"F0.wireOp",EDGE,"E15"),sQuery(id+"F0.wireOp",EDGE,"E17.filletArc"),sQuery(id+"F0.wireOp",EDGE,"E18.filletArc"),sQuery(id+"F0.wireOp",EDGE,"E19.filletArc"),sQuery(id+"F0.wireOp",EDGE,"E20.filletArc"),sQuery(id+"F0.wireOp",EDGE,"E25.0"),sQuery(id+"F0.wireOp",EDGE,"E25.1"),sQuery(id+"F0.wireOp",EDGE,"E25.2"),sQuery(id+"F0.wireOp",EDGE,"E25.3"),sQuery(id+"F0.wireOp",EDGE,"E25.4"),sQuery(id+"F0.wireOp",EDGE,"E25.5"),sQuery(id+"F0.wireOp",EDGE,"E25.6"),sQuery(id+"F0.wireOp",EDGE,"E25.7")])],"isStart":false});
            extrude(context, id + "F17", {"entities" : qUnion([Q0]), "endBound" : BoundingType.UP_TO_SURFACE, "depth" : 25 * mm, "endBoundEntityFace" : qUnion([Q1]), "offsetDistance" : 25 * mm});
        }
    });
